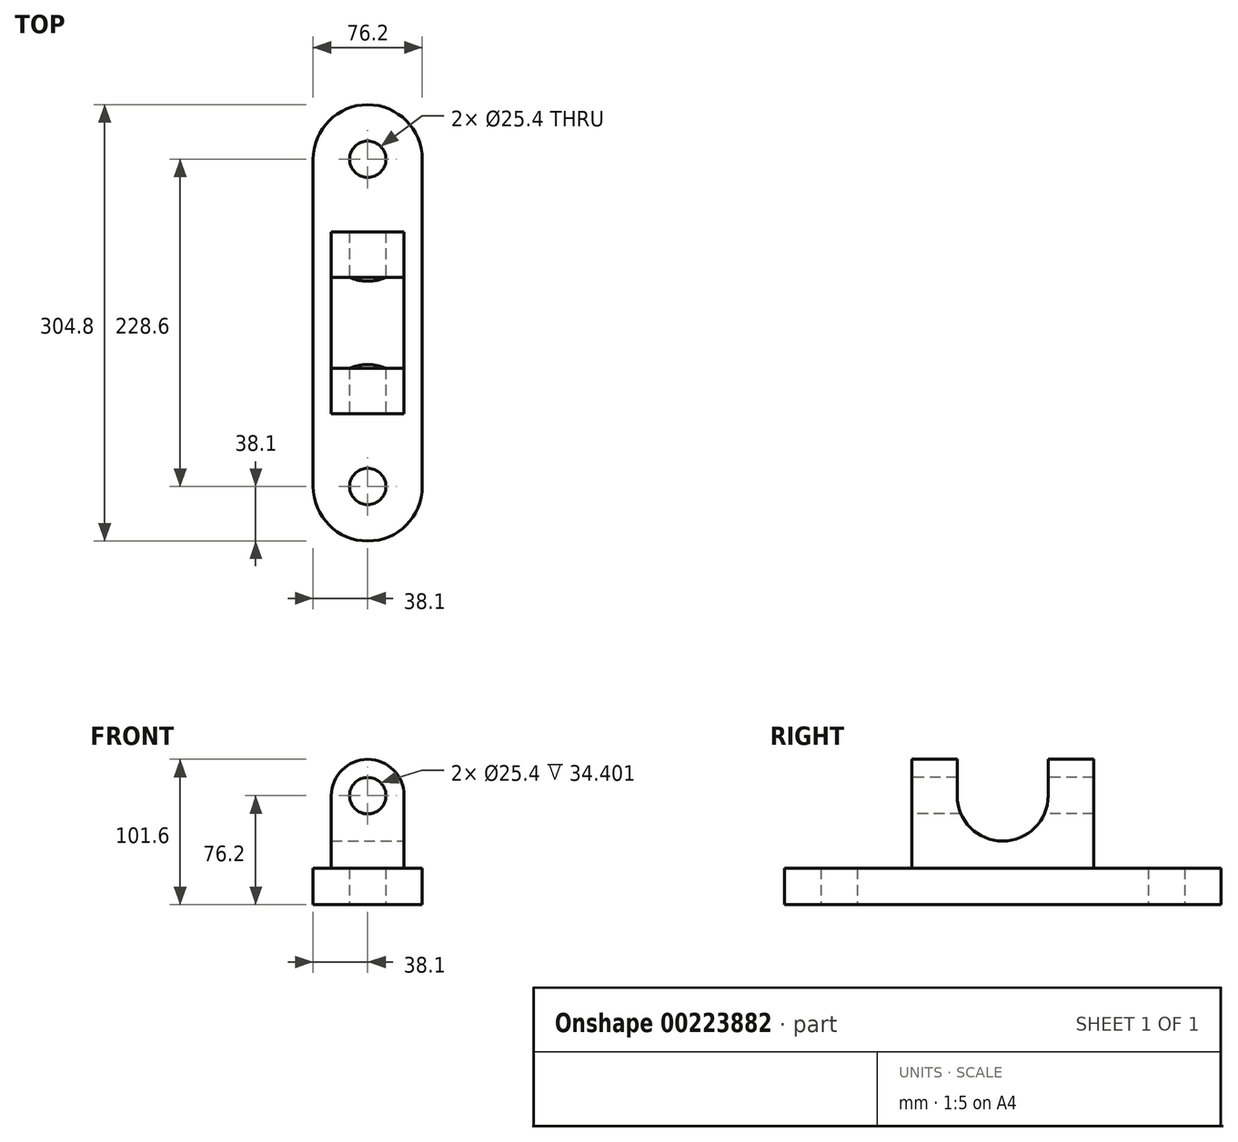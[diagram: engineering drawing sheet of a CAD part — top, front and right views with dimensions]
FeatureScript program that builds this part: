
annotation { "Feature Type Name" : "Feature", "Feature Type Description" : "" }
export const myFeature = defineFeature(function(context is Context, id is Id, definition is map)
    precondition{}
    {
        {
            var Q0;
            Q0=qCreatedBy(makeId("Top.planeOp"),FACE);
            var sketch = newSketch(context, id + "F0", { "sketchPlane" : qUnion([Q0])});
            skLineSegment(sketch, "E0.left", {"start": v(38.1, -114.3) * mm, "end": v(38.1, 114.3) * mm});
            skLineSegment(sketch, "E0.right", {"start": v(-38.1, -114.3) * mm, "end": v(-38.1, 114.3) * mm});
            skPoint(sketch, "E0.middle", {"position": v(0, 0) * mm});
            skArc(sketch, "E1", {"start": v(-38.1, -114.3) * mm, "mid": v(0, -152.4) * mm, "end": v(38.1, -114.3) * mm});
            skArc(sketch, "E2", {"start": v(38.1, 114.3) * mm, "mid": v(0, 152.4) * mm, "end": v(-38.1, 114.3) * mm});
            skCircle(sketch, "E3", {"center": v(0, -114.3) * mm, "radius": 12.7 * mm});
            skCircle(sketch, "E4", {"center": v(0, 114.3) * mm, "radius": 12.7 * mm});
            skSolve(sketch);
        }
        {
            var Q0;
            Q0=makeQuery(id+"F0.imprint","IMPRINT",FACE,{"disambiguationData":[TD([[makeQuery(id+"F0.imprint","IMPRINT",EDGE,{"derivedFrom":sQuery(id+"F0.wireOp",EDGE,"E0.left")}),1.0]])]});
            extrude(context, id + "F1", {"entities" : qUnion([Q0]), "depth" : 25.4 * mm});
        }
        {
            var Q0;
            Q0=makeQuery(id+"F1.opExtrude","CAP_FACE",FACE,{"disambiguationData":[OSD([sQuery(id+"F0.wireOp",EDGE,"E0.left"),sQuery(id+"F0.wireOp",EDGE,"E0.right"),sQuery(id+"F0.wireOp",EDGE,"E1"),sQuery(id+"F0.wireOp",EDGE,"E2"),sQuery(id+"F0.wireOp",EDGE,"E3"),sQuery(id+"F0.wireOp",EDGE,"E4")])],"isStart":false});
            var sketch = newSketch(context, id + "F2", { "sketchPlane" : qUnion([Q0])});
            skLineSegment(sketch, "E5.bottom", {"start": v(25.4, -63.5) * mm, "end": v(-25.4, -63.5) * mm});
            skLineSegment(sketch, "E5.top", {"start": v(25.4, 63.5) * mm, "end": v(-25.4, 63.5) * mm});
            skLineSegment(sketch, "E5.left", {"start": v(25.4, -63.5) * mm, "end": v(25.4, 63.5) * mm});
            skLineSegment(sketch, "E5.right", {"start": v(-25.4, -63.5) * mm, "end": v(-25.4, 63.5) * mm});
            skPoint(sketch, "E5.middle", {"position": v(0, 0) * mm});
            skSolve(sketch);
        }
        {
            var Q0;
            Q0 = qSketchRegion(id + "F2", true);
            extrude(context, id + "F3", {"entities" : qUnion([Q0]), "operationType" : NewBodyOperationType.ADD, "depth" : 50.8 * mm});
        }
        {
            var Q0;
            Q0=makeQuery(id+"F3.opExtrude","SWEPT_FACE",FACE,{"disambiguationData":[OSD([sQuery(id+"F2.wireOp",EDGE,"E5.bottom")])]});
            var sketch = newSketch(context, id + "F4", { "sketchPlane" : qUnion([Q0])});
            skCircle(sketch, "E6", {"center": v(0, 76.2) * mm, "radius": 25.4 * mm});
            skSolve(sketch);
        }
        {
            var Q0;
            {var subQ1=sQuery(id+"F2.wireOp",EDGE,"E5.bottom");var subQ2=makeQuery(id+"F3.opExtrude","CAP_EDGE",EDGE,{"disambiguationData":[OSD([subQ1])],"isStart":false});Q0=makeQuery(id+"F4.imprint","IMPRINT",FACE,{"disambiguationData":[TD([[makeQuery(id+"F4.imprint","IMPRINT",EDGE,{"derivedFrom":subQ2}),-1.0]])]});}
            extrude(context, id + "F5", {"entities" : qUnion([Q0]), "operationType" : NewBodyOperationType.ADD, "oppositeDirection" : true, "depth" : 127 * mm});
        }
        {
            var Q0;
            {var subQ0=sQuery(id+"F2.wireOp",EDGE,"E5.bottom");Q0=makeQuery(id+"F5.boolean.opBoolean","MERGE",FACE,{"derivedFrom":[makeQuery(id+"F3.opExtrude","SWEPT_FACE",FACE,{"disambiguationData":[OSD([subQ0])]}),makeQuery(id+"F5.opExtrude","CAP_FACE",FACE,{"disambiguationData":[OSD([subQ0,sQuery(id+"F4.wireOp",EDGE,"E6")])],"isStart":true})]});}
            var sketch = newSketch(context, id + "F6", { "sketchPlane" : qUnion([Q0])});
            skCircle(sketch, "E7", {"center": v(0, 76.2) * mm, "radius": 12.7 * mm});
            skSolve(sketch);
        }
        {
            var Q0;
            Q0=makeQuery(id+"F6.imprint","IMPRINT",FACE,{"disambiguationData":[TD([[makeQuery(id+"F6.imprint","IMPRINT",EDGE,{"derivedFrom":sQuery(id+"F6.wireOp",EDGE,"E7")}),1.0]])]});
            extrude(context, id + "F7", {"entities" : qUnion([Q0]), "operationType" : NewBodyOperationType.REMOVE, "oppositeDirection" : true, "depth" : 127 * mm});
        }
        {
            var Q0;
            Q0=makeQuery(id+"F3.opExtrude","SWEPT_FACE",FACE,{"disambiguationData":[OSD([sQuery(id+"F2.wireOp",EDGE,"E5.left")])]});
            var sketch = newSketch(context, id + "F8", { "sketchPlane" : qUnion([Q0])});
            skPoint(sketch, "E8.middle", {"position": v(0, 76.2) * mm});
            skArc(sketch, "E9", {"start": v(-31.75, 76.2) * mm, "mid": v(0, 44.45) * mm, "end": v(31.75, 76.2) * mm});
            skLineSegment(sketch, "E10.bottom", {"start": v(31.75, 76.2) * mm, "end": v(-31.75, 76.2) * mm});
            skLineSegment(sketch, "E10.top", {"start": v(31.75, 139.7) * mm, "end": v(-31.75, 139.7) * mm});
            skLineSegment(sketch, "E10.left", {"start": v(31.75, 76.2) * mm, "end": v(31.75, 139.7) * mm});
            skLineSegment(sketch, "E10.right", {"start": v(-31.75, 76.2) * mm, "end": v(-31.75, 139.7) * mm});
            skPoint(sketch, "E10.middle", {"position": v(0, 107.95) * mm});
            skSolve(sketch);
        }
        {
            var Q0;
            Q0 = qSketchRegion(id + "F8", true);
            extrude(context, id + "F9", {"entities" : qUnion([Q0]), "operationType" : NewBodyOperationType.REMOVE, "oppositeDirection" : true, "depth" : 76.2 * mm});
        }
    });
